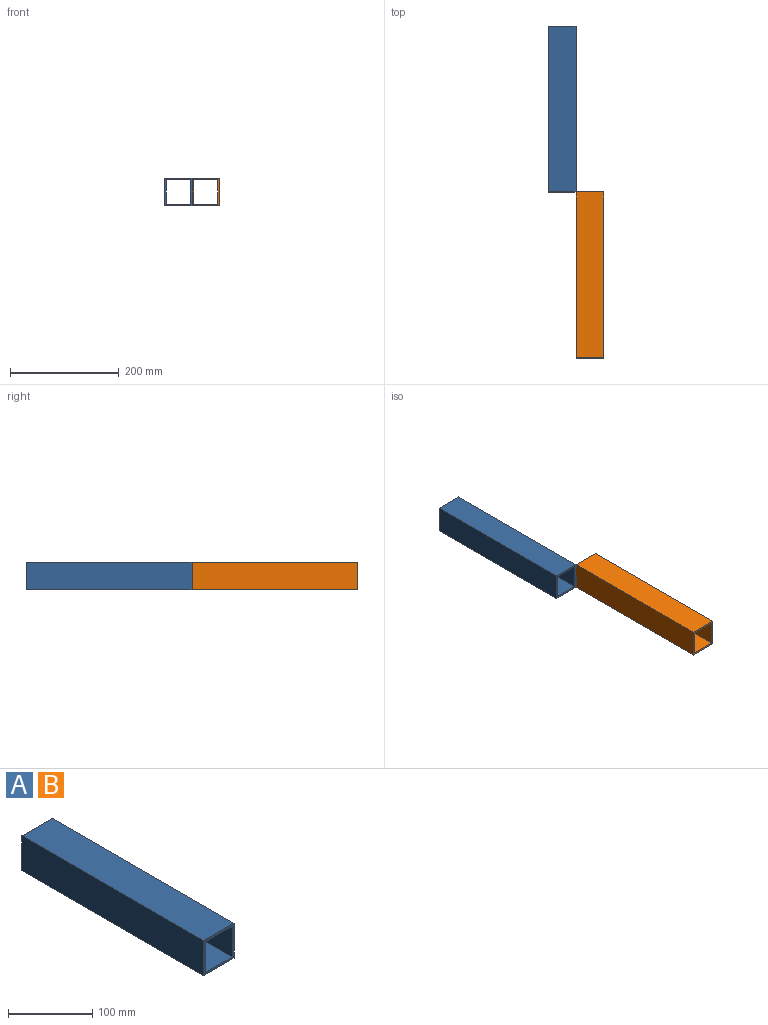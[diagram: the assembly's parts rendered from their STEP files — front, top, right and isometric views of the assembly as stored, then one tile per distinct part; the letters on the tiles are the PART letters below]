
ASSEMBLY  parts=2 mates=1
PART A: 10 faces, bbox 50.8x304.8x50.8 mm
  f0: plane 304.8x50.8mm, normal (0,0,-1), area 15483.8mm2, adj f1,f7,f8,f9
  f1: plane 304.8x50.8mm, normal (1,0,0), area 15483.8mm2, adj f0,f2,f8,f9
  f2: plane 304.8x50.8mm, normal (0,0,1), area 15483.8mm2, adj f1,f7,f8,f9
  f3: plane 304.8x44.45mm, normal (0,0,1), area 13548.4mm2, adj f4,f6,f8,f9
  f4: plane 304.8x44.45mm, normal (1,0,0), area 13548.4mm2, adj f3,f5,f8,f9
  f5: plane 304.8x44.45mm, normal (0,0,-1), area 13548.4mm2, adj f4,f6,f8,f9
  f6: plane 304.8x44.45mm, normal (-1,0,0), area 13548.4mm2, adj f3,f5,f8,f9
  f7: plane 304.8x50.8mm, normal (-1,0,0), area 15483.8mm2, adj f0,f2,f8,f9
  f8: plane 50.8x50.8mm, normal (0,-1,0), area 604.8mm2, adj f0,f1,f2,f3,f4,f5,f6,f7
  f9: plane 50.8x50.8mm, normal (0,1,0), area 604.8mm2, adj f0,f1,f2,f3,f4,f5,f6,f7
PART B: same geometry as A
PLACE A t=(-82.15,60.49,-66.71)mm
PLACE B rot(axis=(0.71,0,-0.71),180deg) t=(-31.35,-549.11,-66.71)mm
MATE planar B.f2 <-> A.f1  axis (-1,0,0) through (-56.75,-244.31,-41.31)mm
